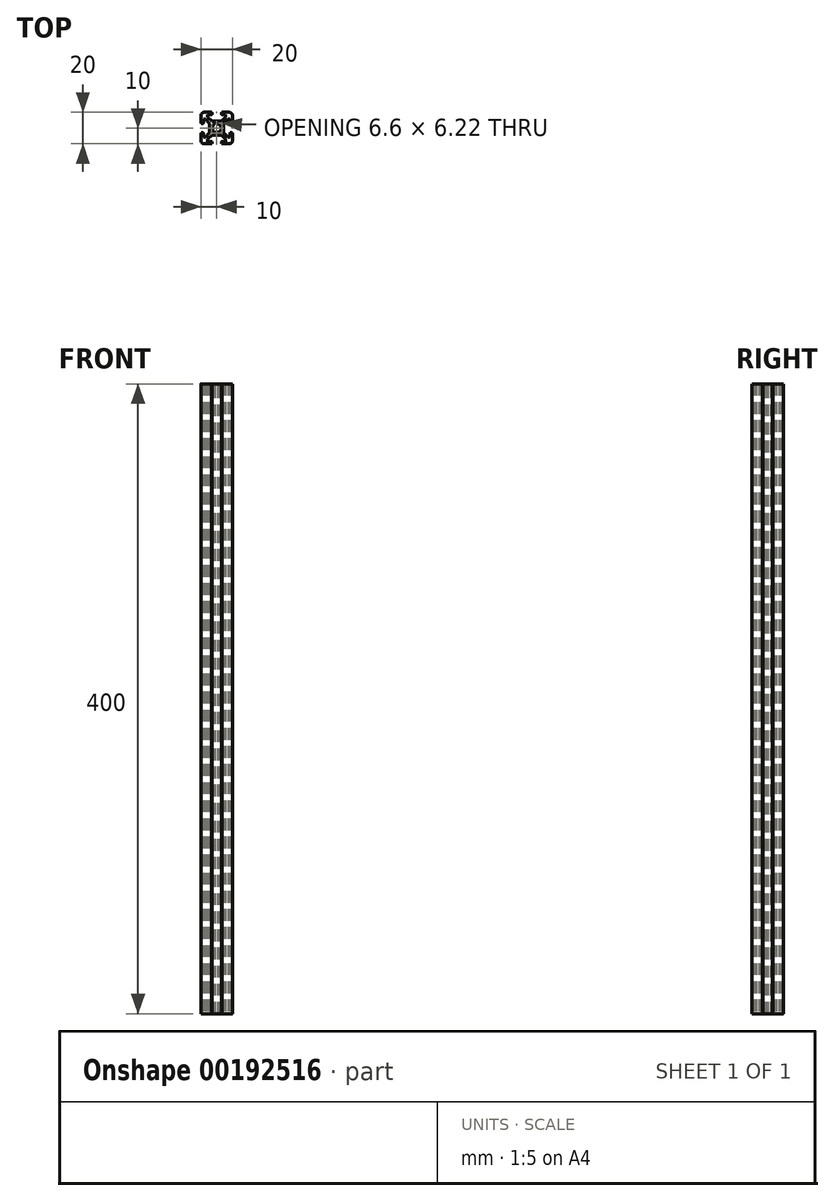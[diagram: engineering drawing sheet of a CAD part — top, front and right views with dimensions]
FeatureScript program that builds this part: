
annotation { "Feature Type Name" : "Feature", "Feature Type Description" : "" }
export const myFeature = defineFeature(function(context is Context, id is Id, definition is map)
    precondition{}
    {
        {
            var Q0;
            Q0=qCreatedBy(makeId("Top.planeOp"),FACE);
            var sketch = newSketch(context, id + "F0", { "sketchPlane" : qUnion([Q0])});
            skLineSegment(sketch, "E0.bottom", {"start": v(-10, 10) * mm, "end": v(10, 10) * mm});
            skLineSegment(sketch, "E0.top", {"start": v(-10, -10) * mm, "end": v(10, -10) * mm});
            skLineSegment(sketch, "E0.left", {"start": v(-10, 10) * mm, "end": v(-10, -10) * mm});
            skLineSegment(sketch, "E0.right", {"start": v(10, 10) * mm, "end": v(10, -10) * mm});
            skSolve(sketch);
        }
        {
            var Q0;
            Q0=qSketchRegion(id+"F0",true);
            extrude(context, id + "F1", {"entities" : qUnion([Q0]), "depth" : 400 * mm});
        }
        {
            var Q0;
            Q0=makeQuery(id+"F1.opExtrude","SWEPT_EDGE",EDGE,{"disambiguationData":[OSD([sQuery(id+"F0.wireOp",EDGE,"E0.bottom"),sQuery(id+"F0.wireOp",EDGE,"E0.right")])]});
            var Q1;
            Q1=makeQuery(id+"F1.opExtrude","SWEPT_EDGE",EDGE,{"disambiguationData":[OSD([sQuery(id+"F0.wireOp",EDGE,"E0.bottom"),sQuery(id+"F0.wireOp",EDGE,"E0.left")])]});
            var Q2;
            Q2=makeQuery(id+"F1.opExtrude","SWEPT_EDGE",EDGE,{"disambiguationData":[OSD([sQuery(id+"F0.wireOp",EDGE,"E0.top"),sQuery(id+"F0.wireOp",EDGE,"E0.left")])]});
            var Q3;
            Q3=makeQuery(id+"F1.opExtrude","SWEPT_EDGE",EDGE,{"disambiguationData":[OSD([sQuery(id+"F0.wireOp",EDGE,"E0.top"),sQuery(id+"F0.wireOp",EDGE,"E0.right")])]});
            fillet(context, id + "F2", {"entities" : qUnion([Q0, Q1, Q2, Q3]), "radius" : 2 * mm, "tangentPropagation" : true, "allowEdgeOverflow" : false});
        }
        {
            var Q0;
            Q0=makeQuery(id+"F1.opExtrude","CAP_FACE",FACE,{"disambiguationData":[OSD([sQuery(id+"F0.wireOp",EDGE,"E0.bottom"),sQuery(id+"F0.wireOp",EDGE,"E0.top"),sQuery(id+"F0.wireOp",EDGE,"E0.left"),sQuery(id+"F0.wireOp",EDGE,"E0.right")])],"isStart":true});
            var sketch = newSketch(context, id + "F3", { "sketchPlane" : qUnion([Q0])});
            skLineSegment(sketch, "E1", {"start": v(-10, 3) * mm, "end": v(-8.5, 3) * mm});
            skLineSegment(sketch, "E2", {"start": v(-8.5, 3) * mm, "end": v(-8.5, 5.63) * mm});
            skLineSegment(sketch, "E3", {"start": v(-8.5, 5.63) * mm, "end": v(-7.13, 5.63) * mm});
            skLineSegment(sketch, "E4", {"start": v(-7.13, 5.63) * mm, "end": v(-4.5, 3) * mm});
            skLineSegment(sketch, "E5", {"start": v(-4.5, 3) * mm, "end": v(-4.5, 0) * mm});
            skLineSegment(sketch, "E6.MirrorCS", {"start": v(-8.5, -5.63) * mm, "end": v(-7.13, -5.63) * mm});
            skLineSegment(sketch, "E7.MirrorCS", {"start": v(-10, -3) * mm, "end": v(-8.5, -3) * mm});
            skLineSegment(sketch, "E8.MirrorCS", {"start": v(-8.5, -3) * mm, "end": v(-8.5, -5.63) * mm});
            skLineSegment(sketch, "E9.MirrorCS", {"start": v(-7.13, -5.63) * mm, "end": v(-4.5, -3) * mm});
            skLineSegment(sketch, "E10.MirrorCS", {"start": v(-4.5, -3) * mm, "end": v(-4.5, 0) * mm});
            skLineSegment(sketch, "E11", {"start": v(0, 15.03) * mm, "end": v(0, -14.36) * mm, "construction": true});
            skLineSegment(sketch, "E12.MirrorCS", {"start": v(8.5, 5.63) * mm, "end": v(7.13, 5.63) * mm});
            skLineSegment(sketch, "E13.MirrorCS", {"start": v(8.5, -5.63) * mm, "end": v(7.13, -5.63) * mm});
            skLineSegment(sketch, "E14.MirrorCS", {"start": v(10, 3) * mm, "end": v(8.5, 3) * mm});
            skLineSegment(sketch, "E15.MirrorCS", {"start": v(8.5, 3) * mm, "end": v(8.5, 5.63) * mm});
            skLineSegment(sketch, "E16.MirrorCS", {"start": v(10, -3) * mm, "end": v(8.5, -3) * mm});
            skLineSegment(sketch, "E17.MirrorCS", {"start": v(7.13, 5.63) * mm, "end": v(4.5, 3) * mm});
            skLineSegment(sketch, "E18.MirrorCS", {"start": v(4.5, -3) * mm, "end": v(4.5, 0) * mm});
            skLineSegment(sketch, "E19.MirrorCS", {"start": v(7.13, -5.63) * mm, "end": v(4.5, -3) * mm});
            skLineSegment(sketch, "E20.MirrorCS", {"start": v(4.5, 3) * mm, "end": v(4.5, 0) * mm});
            skLineSegment(sketch, "E21.MirrorCS", {"start": v(8.5, -3) * mm, "end": v(8.5, -5.63) * mm});
            skLineSegment(sketch, "E22", {"start": v(-9.41, 9.41) * mm, "end": v(3, -3) * mm, "construction": true});
            skLineSegment(sketch, "E23.MirrorCS", {"start": v(-5.63, -8.5) * mm, "end": v(-5.63, -7.13) * mm});
            skLineSegment(sketch, "E24.MirrorCS", {"start": v(5.63, -8.5) * mm, "end": v(5.63, -7.13) * mm});
            skLineSegment(sketch, "E25.MirrorCS", {"start": v(-3, -10) * mm, "end": v(-3, -8.5) * mm});
            skLineSegment(sketch, "E26.MirrorCS", {"start": v(3, -10) * mm, "end": v(3, -8.5) * mm});
            skLineSegment(sketch, "E27.MirrorCS", {"start": v(-5.63, -7.13) * mm, "end": v(-3, -4.5) * mm});
            skLineSegment(sketch, "E28.MirrorCS", {"start": v(-3, -8.5) * mm, "end": v(-5.63, -8.5) * mm});
            skLineSegment(sketch, "E29.MirrorCS", {"start": v(3, -8.5) * mm, "end": v(5.63, -8.5) * mm});
            skLineSegment(sketch, "E30.MirrorCS", {"start": v(3, -4.5) * mm, "end": v(0, -4.5) * mm});
            skLineSegment(sketch, "E31.MirrorCS", {"start": v(-3, -4.5) * mm, "end": v(0, -4.5) * mm});
            skLineSegment(sketch, "E32.MirrorCS", {"start": v(5.63, -7.13) * mm, "end": v(3, -4.5) * mm});
            skLineSegment(sketch, "E33.MirrorCS", {"start": v(-15.03, 0) * mm, "end": v(14.36, 0) * mm, "construction": true});
            skLineSegment(sketch, "E34.MirrorCS", {"start": v(5.63, 7.13) * mm, "end": v(3, 4.5) * mm});
            skLineSegment(sketch, "E35.MirrorCS", {"start": v(-5.63, 7.13) * mm, "end": v(-3, 4.5) * mm});
            skLineSegment(sketch, "E36.MirrorCS", {"start": v(-3, 4.5) * mm, "end": v(0, 4.5) * mm});
            skLineSegment(sketch, "E37.MirrorCS", {"start": v(3, 4.5) * mm, "end": v(0, 4.5) * mm});
            skLineSegment(sketch, "E38.MirrorCS", {"start": v(-5.63, 8.5) * mm, "end": v(-5.63, 7.13) * mm});
            skLineSegment(sketch, "E39.MirrorCS", {"start": v(5.63, 8.5) * mm, "end": v(5.63, 7.13) * mm});
            skLineSegment(sketch, "E40.MirrorCS", {"start": v(3, 10) * mm, "end": v(3, 8.5) * mm});
            skLineSegment(sketch, "E41.MirrorCS", {"start": v(-3, 10) * mm, "end": v(-3, 8.5) * mm});
            skLineSegment(sketch, "E42.MirrorCS", {"start": v(3, 8.5) * mm, "end": v(5.63, 8.5) * mm});
            skLineSegment(sketch, "E43.MirrorCS", {"start": v(-3, 8.5) * mm, "end": v(-5.63, 8.5) * mm});
            skSolve(sketch);
        }
        {
            var Q0;
            Q0=qSketchRegion(id+"F3",true);
            var Q1;
            Q1=makeQuery(id+"F3.imprint","IMPRINT",FACE,{"disambiguationData":[TD([[makeQuery(id+"F3.imprint","IMPRINT",EDGE,{"derivedFrom":sQuery(id+"F3.wireOp",EDGE,"E35.MirrorCS")}),1.0]])]});
            var Q2;
            Q2=makeQuery(id+"F3.imprint","IMPRINT",FACE,{"disambiguationData":[TD([[makeQuery(id+"F3.imprint","IMPRINT",EDGE,{"derivedFrom":sQuery(id+"F3.wireOp",EDGE,"E20.MirrorCS")}),1.0]])]});
            var Q3;
            Q3=makeQuery(id+"F3.imprint","IMPRINT",FACE,{"disambiguationData":[TD([[makeQuery(id+"F3.imprint","IMPRINT",EDGE,{"derivedFrom":sQuery(id+"F3.wireOp",EDGE,"E23.MirrorCS")}),-1.0]])]});
            var Q4;
            {var subQ0=sQuery(id+"F3.wireOp",EDGE,"E1");Q4=makeQuery(id+"F3.imprint","IMPRINT",FACE,{"disambiguationData":[TD([[makeQuery(id+"F3.imprint","IMPRINT",EDGE,{"derivedFrom":subQ0}),-1.0]])]});}
            extrude(context, id + "F4", {"entities" : qUnion([Q0, Q1, Q2, Q3, Q4]), "operationType" : NewBodyOperationType.REMOVE, "endBound" : BoundingType.UP_TO_NEXT, "oppositeDirection" : true, "depth" : 25.4 * mm});
        }
        {
            var Q0;
            Q0=makeQuery(id+"F1.opExtrude","CAP_FACE",FACE,{"disambiguationData":[OSD([sQuery(id+"F0.wireOp",EDGE,"E0.bottom"),sQuery(id+"F0.wireOp",EDGE,"E0.top"),sQuery(id+"F0.wireOp",EDGE,"E0.left"),sQuery(id+"F0.wireOp",EDGE,"E0.right")])],"isStart":false});
            var sketch = newSketch(context, id + "F5", { "sketchPlane" : qUnion([Q0])});
            skArc(sketch, "E44", {"start": v(-2.68, -0.6) * mm, "mid": v(-2.38, -1.37) * mm, "end": v(-1.87, -2.02) * mm});
            skLineSegment(sketch, "E45", {"start": v(-7.32, 0) * mm, "end": v(15.13, 0) * mm, "construction": true});
            skPoint(sketch, "E45.endSnap0", {"position": v(-4.5, 0) * mm});
            skLineSegment(sketch, "E46", {"start": v(-3.3, 0.5) * mm, "end": v(-3.3, 0) * mm});
            skLineSegment(sketch, "E47", {"start": v(-3.3, 0.5) * mm, "end": v(-2.68, 0.6) * mm});
            skLineSegment(sketch, "E48.MirrorCS", {"start": v(-3.3, -0.5) * mm, "end": v(-2.68, -0.6) * mm});
            skLineSegment(sketch, "E49.MirrorCS", {"start": v(-3.3, -0.5) * mm, "end": v(-3.3, 0) * mm});
            skLineSegment(sketch, "E50", {"start": v(0, 3.17) * mm, "end": v(0, -3.5) * mm, "construction": true});
            skLineSegment(sketch, "E51.MirrorCS", {"start": v(3.3, -0.5) * mm, "end": v(2.68, -0.6) * mm});
            skLineSegment(sketch, "E52.MirrorCS", {"start": v(3.3, -0.5) * mm, "end": v(3.3, 0) * mm});
            skLineSegment(sketch, "E53.MirrorCS", {"start": v(3.3, 0.5) * mm, "end": v(2.68, 0.6) * mm});
            skLineSegment(sketch, "E54.MirrorCS", {"start": v(3.3, 0.5) * mm, "end": v(3.3, 0) * mm});
            skArc(sketch, "E55.trimOffspring", {"start": v(2.68, 0.6) * mm, "mid": v(2.38, 1.38) * mm, "end": v(1.87, 2.02) * mm});
            skLineSegment(sketch, "E56", {"start": v(-2.57, 4.46) * mm, "end": v(0, 0) * mm, "construction": true});
            skLineSegment(sketch, "E57", {"start": v(0, 0) * mm, "end": v(2.15, 3.72) * mm, "construction": true});
            skLineSegment(sketch, "E58.MirrorCS", {"start": v(-2.08, 2.6) * mm, "end": v(-1.87, 2.02) * mm});
            skLineSegment(sketch, "E59.MirrorCS", {"start": v(-2.08, 2.6) * mm, "end": v(-1.65, 2.86) * mm});
            skLineSegment(sketch, "E60.MirrorCS", {"start": v(-1.22, 3.1) * mm, "end": v(-0.81, 2.63) * mm});
            skLineSegment(sketch, "E61.MirrorCS", {"start": v(-1.22, 3.1) * mm, "end": v(-1.65, 2.86) * mm});
            skLineSegment(sketch, "E62.MirrorCS", {"start": v(2.08, -2.6) * mm, "end": v(1.87, -2.02) * mm});
            skLineSegment(sketch, "E63.MirrorCS", {"start": v(5.15, 0) * mm, "end": v(0, 0) * mm, "construction": true});
            skLineSegment(sketch, "E64.MirrorCS", {"start": v(1.22, -3.1) * mm, "end": v(0.81, -2.63) * mm});
            skLineSegment(sketch, "E65.MirrorCS", {"start": v(1.22, -3.1) * mm, "end": v(1.65, -2.86) * mm});
            skLineSegment(sketch, "E66.MirrorCS", {"start": v(2.08, -2.6) * mm, "end": v(1.65, -2.86) * mm});
            skLineSegment(sketch, "E67.MirrorCS", {"start": v(2.08, 2.6) * mm, "end": v(1.87, 2.02) * mm});
            skLineSegment(sketch, "E68.MirrorCS", {"start": v(2.08, 2.6) * mm, "end": v(1.65, 2.86) * mm});
            skLineSegment(sketch, "E69.MirrorCS", {"start": v(1.22, 3.1) * mm, "end": v(0.81, 2.63) * mm});
            skLineSegment(sketch, "E70.MirrorCS", {"start": v(1.22, 3.1) * mm, "end": v(1.65, 2.86) * mm});
            skLineSegment(sketch, "E71.MirrorCS", {"start": v(-2.08, -2.6) * mm, "end": v(-1.65, -2.86) * mm});
            skLineSegment(sketch, "E72.MirrorCS", {"start": v(-1.22, -3.1) * mm, "end": v(-1.65, -2.86) * mm});
            skLineSegment(sketch, "E73.MirrorCS", {"start": v(-2.08, -2.6) * mm, "end": v(-1.87, -2.02) * mm});
            skLineSegment(sketch, "E74.MirrorCS", {"start": v(-1.22, -3.1) * mm, "end": v(-0.81, -2.63) * mm});
            skArc(sketch, "E75.trimOffspring", {"start": v(-1.87, 2.02) * mm, "mid": v(-2.38, 1.37) * mm, "end": v(-2.68, 0.6) * mm});
            skArc(sketch, "E76.trimOffspring", {"start": v(0.81, 2.63) * mm, "mid": v(0, 2.75) * mm, "end": v(-0.81, 2.63) * mm});
            skArc(sketch, "E77.trimOffspring", {"start": v(1.87, -2.02) * mm, "mid": v(2.38, -1.37) * mm, "end": v(2.68, -0.6) * mm});
            skArc(sketch, "E78.trimOffspring", {"start": v(-0.81, -2.63) * mm, "mid": v(0, -2.75) * mm, "end": v(0.81, -2.63) * mm});
            skSolve(sketch);
        }
        {
            var Q0;
            Q0=qSketchRegion(id+"F5",true);
            extrude(context, id + "F6", {"entities" : qUnion([Q0]), "operationType" : NewBodyOperationType.REMOVE, "endBound" : BoundingType.UP_TO_NEXT, "oppositeDirection" : true, "depth" : 25.4 * mm});
        }
        {
            var Q0;
            Q0=makeQuery(id+"F1.opExtrude","CAP_FACE",FACE,{"disambiguationData":[OSD([sQuery(id+"F0.wireOp",EDGE,"E0.bottom"),sQuery(id+"F0.wireOp",EDGE,"E0.top"),sQuery(id+"F0.wireOp",EDGE,"E0.left"),sQuery(id+"F0.wireOp",EDGE,"E0.right")])],"isStart":true});
            var sketch = newSketch(context, id + "F7", { "sketchPlane" : qUnion([Q0])});
            skLineSegment(sketch, "E79.bottom", {"start": v(-10, 3) * mm, "end": v(-9.75, 3) * mm});
            skLineSegment(sketch, "E79.top", {"start": v(-10, 3.25) * mm, "end": v(-9.75, 3.25) * mm});
            skLineSegment(sketch, "E79.left", {"start": v(-10, 3) * mm, "end": v(-10, 3.25) * mm});
            skLineSegment(sketch, "E79.right", {"start": v(-9.75, 3) * mm, "end": v(-9.75, 3.25) * mm});
            skLineSegment(sketch, "E80", {"start": v(0, 12.33) * mm, "end": v(0, -11.82) * mm, "construction": true});
            skLineSegment(sketch, "E81", {"start": v(-12.76, 0) * mm, "end": v(11.5, 0) * mm, "construction": true});
            skLineSegment(sketch, "E82", {"start": v(-10, 10) * mm, "end": v(10.81, -10.81) * mm, "construction": true});
            skLineSegment(sketch, "E83", {"start": v(-9.41, -9.41) * mm, "end": v(9.41, 9.41) * mm, "construction": true});
            skLineSegment(sketch, "E84.MirrorCS", {"start": v(-3.25, 10) * mm, "end": v(-3.25, 9.75) * mm});
            skLineSegment(sketch, "E85.MirrorCS", {"start": v(-3, 10) * mm, "end": v(-3, 9.75) * mm});
            skLineSegment(sketch, "E86.MirrorCS", {"start": v(-3, 9.75) * mm, "end": v(-3.25, 9.75) * mm});
            skLineSegment(sketch, "E87.MirrorCS", {"start": v(-3, 10) * mm, "end": v(-3.25, 10) * mm});
            skLineSegment(sketch, "E88.MirrorCS", {"start": v(3.25, 10) * mm, "end": v(3.25, 9.75) * mm});
            skLineSegment(sketch, "E89.MirrorCS", {"start": v(3, 10) * mm, "end": v(3, 9.75) * mm});
            skLineSegment(sketch, "E90.MirrorCS", {"start": v(3, 10) * mm, "end": v(3.25, 10) * mm});
            skLineSegment(sketch, "E91.MirrorCS", {"start": v(3, 9.75) * mm, "end": v(3.25, 9.75) * mm});
            skLineSegment(sketch, "E92.MirrorCS", {"start": v(10, 3.25) * mm, "end": v(9.75, 3.25) * mm});
            skLineSegment(sketch, "E93.MirrorCS", {"start": v(10, 3) * mm, "end": v(10, 3.25) * mm});
            skLineSegment(sketch, "E94.MirrorCS", {"start": v(9.75, 3) * mm, "end": v(9.75, 3.25) * mm});
            skLineSegment(sketch, "E95.MirrorCS", {"start": v(10, 3) * mm, "end": v(9.75, 3) * mm});
            skLineSegment(sketch, "E96.MirrorCS", {"start": v(-10, -3.25) * mm, "end": v(-9.75, -3.25) * mm});
            skLineSegment(sketch, "E97.MirrorCS", {"start": v(-10, -3) * mm, "end": v(-10, -3.25) * mm});
            skLineSegment(sketch, "E98.MirrorCS", {"start": v(-9.75, -3) * mm, "end": v(-9.75, -3.25) * mm});
            skLineSegment(sketch, "E99.MirrorCS", {"start": v(-10, -3) * mm, "end": v(-9.75, -3) * mm});
            skLineSegment(sketch, "E100.MirrorCS", {"start": v(10, -3.25) * mm, "end": v(9.75, -3.25) * mm});
            skLineSegment(sketch, "E101.MirrorCS", {"start": v(10, -3) * mm, "end": v(10, -3.25) * mm});
            skLineSegment(sketch, "E102.MirrorCS", {"start": v(10, -3) * mm, "end": v(9.75, -3) * mm});
            skLineSegment(sketch, "E103.MirrorCS", {"start": v(9.75, -3) * mm, "end": v(9.75, -3.25) * mm});
            skLineSegment(sketch, "E104.MirrorCS", {"start": v(-3.25, -10) * mm, "end": v(-3.25, -9.75) * mm});
            skLineSegment(sketch, "E105.MirrorCS", {"start": v(-3, -10) * mm, "end": v(-3, -9.75) * mm});
            skLineSegment(sketch, "E106.MirrorCS", {"start": v(3, -10) * mm, "end": v(3.25, -10) * mm});
            skLineSegment(sketch, "E107.MirrorCS", {"start": v(-3, -9.75) * mm, "end": v(-3.25, -9.75) * mm});
            skLineSegment(sketch, "E108.MirrorCS", {"start": v(-3, -10) * mm, "end": v(-3.25, -10) * mm});
            skLineSegment(sketch, "E109.MirrorCS", {"start": v(3, -10) * mm, "end": v(3, -9.75) * mm});
            skLineSegment(sketch, "E110.MirrorCS", {"start": v(3.25, -10) * mm, "end": v(3.25, -9.75) * mm});
            skLineSegment(sketch, "E111.MirrorCS", {"start": v(3, -9.75) * mm, "end": v(3.25, -9.75) * mm});
            skSolve(sketch);
        }
        {
            var Q0;
            Q0=qSketchRegion(id+"F7",true);
            extrude(context, id + "F8", {"entities" : qUnion([Q0]), "operationType" : NewBodyOperationType.REMOVE, "endBound" : BoundingType.UP_TO_NEXT, "oppositeDirection" : true, "depth" : 25.4 * mm});
        }
        {
            var Q0;
            Q0=makeQuery(id+"F4.boolean.opBoolean","COPY",EDGE,{"derivedFrom":makeQuery(id+"F4.opExtrude","SWEPT_EDGE",EDGE,{"disambiguationData":[OSD([sQuery(id+"F3.wireOp",EDGE,"E7.MirrorCS"),sQuery(id+"F3.wireOp",EDGE,"E8.MirrorCS")])]})});
            var Q1;
            Q1=makeQuery(id+"F4.boolean.opBoolean","COPY",EDGE,{"derivedFrom":makeQuery(id+"F4.opExtrude","SWEPT_EDGE",EDGE,{"disambiguationData":[OSD([sQuery(id+"F3.wireOp",EDGE,"E1"),sQuery(id+"F3.wireOp",EDGE,"E2")])]})});
            var Q2;
            Q2=makeQuery(id+"F4.boolean.opBoolean","COPY",EDGE,{"derivedFrom":makeQuery(id+"F4.opExtrude","SWEPT_EDGE",EDGE,{"disambiguationData":[OSD([sQuery(id+"F3.wireOp",EDGE,"E41.MirrorCS"),sQuery(id+"F3.wireOp",EDGE,"E43.MirrorCS")])]})});
            var Q3;
            Q3=makeQuery(id+"F4.boolean.opBoolean","COPY",EDGE,{"derivedFrom":makeQuery(id+"F4.opExtrude","SWEPT_EDGE",EDGE,{"disambiguationData":[OSD([sQuery(id+"F3.wireOp",EDGE,"E40.MirrorCS"),sQuery(id+"F3.wireOp",EDGE,"E42.MirrorCS")])]})});
            var Q4;
            Q4=makeQuery(id+"F4.boolean.opBoolean","COPY",EDGE,{"derivedFrom":makeQuery(id+"F4.opExtrude","SWEPT_EDGE",EDGE,{"disambiguationData":[OSD([sQuery(id+"F3.wireOp",EDGE,"E14.MirrorCS"),sQuery(id+"F3.wireOp",EDGE,"E15.MirrorCS")])]})});
            var Q5;
            Q5=makeQuery(id+"F4.boolean.opBoolean","COPY",EDGE,{"derivedFrom":makeQuery(id+"F4.opExtrude","SWEPT_EDGE",EDGE,{"disambiguationData":[OSD([sQuery(id+"F3.wireOp",EDGE,"E25.MirrorCS"),sQuery(id+"F3.wireOp",EDGE,"E28.MirrorCS")])]})});
            var Q6;
            Q6=makeQuery(id+"F4.boolean.opBoolean","COPY",EDGE,{"derivedFrom":makeQuery(id+"F4.opExtrude","SWEPT_EDGE",EDGE,{"disambiguationData":[OSD([sQuery(id+"F3.wireOp",EDGE,"E26.MirrorCS"),sQuery(id+"F3.wireOp",EDGE,"E29.MirrorCS")])]})});
            var Q7;
            Q7=makeQuery(id+"F4.boolean.opBoolean","COPY",EDGE,{"derivedFrom":makeQuery(id+"F4.opExtrude","SWEPT_EDGE",EDGE,{"disambiguationData":[OSD([sQuery(id+"F3.wireOp",EDGE,"E16.MirrorCS"),sQuery(id+"F3.wireOp",EDGE,"E21.MirrorCS")])]})});
            fillet(context, id + "F9", {"entities" : qUnion([Q0, Q1, Q2, Q3, Q4, Q5, Q6, Q7]), "radius" : 0.25 * mm, "tangentPropagation" : true, "allowEdgeOverflow" : false});
        }
    });
